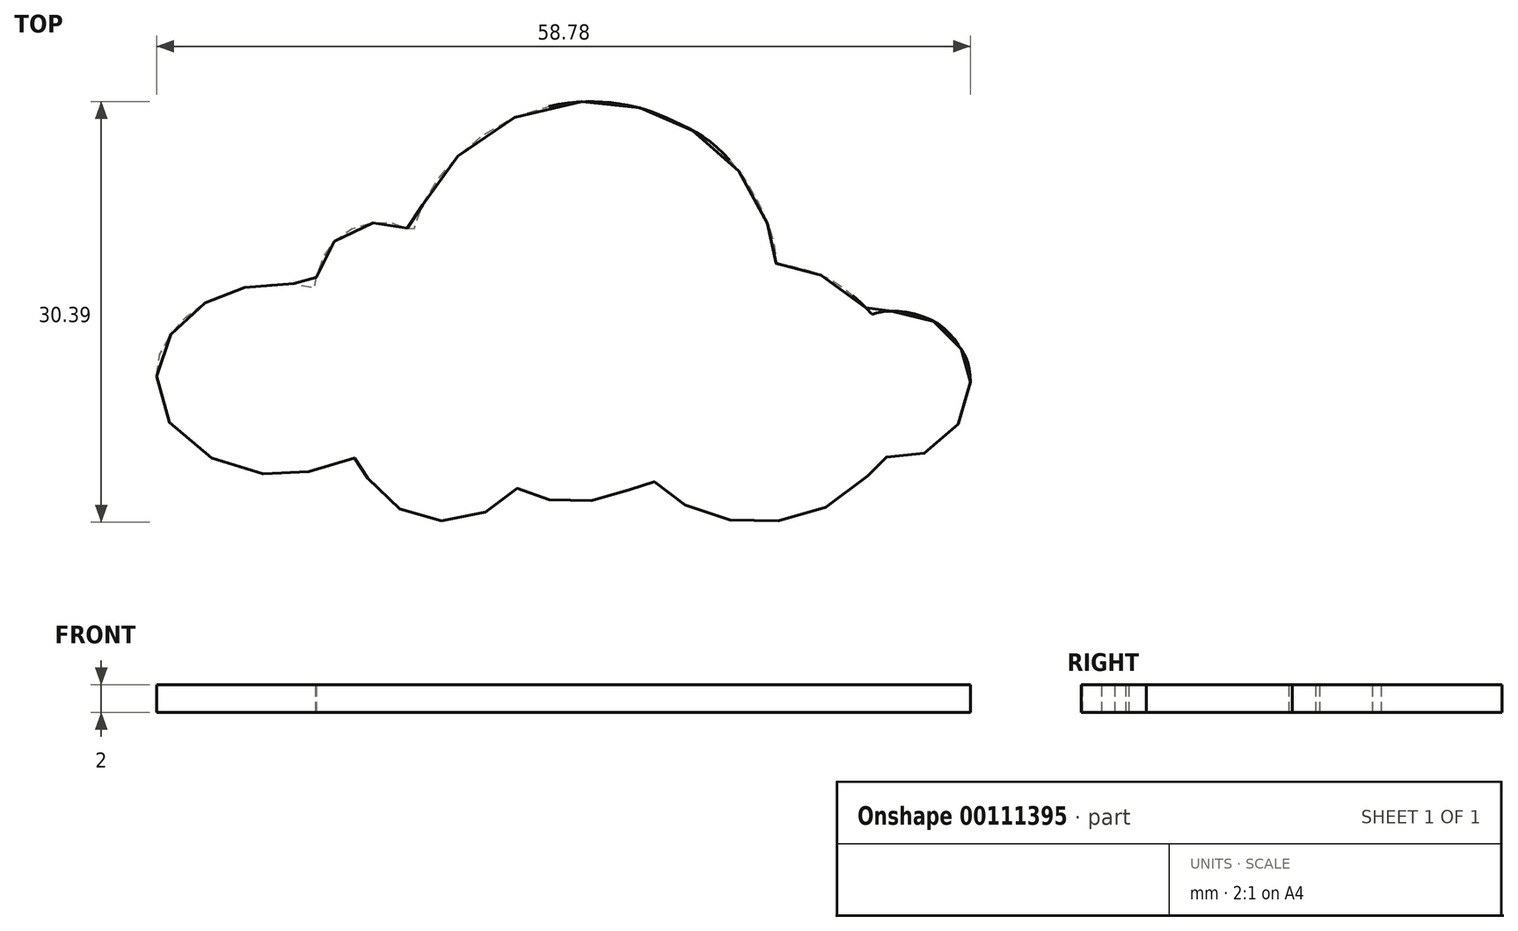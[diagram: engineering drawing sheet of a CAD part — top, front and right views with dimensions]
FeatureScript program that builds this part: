
annotation { "Feature Type Name" : "Feature", "Feature Type Description" : "" }
export const myFeature = defineFeature(function(context is Context, id is Id, definition is map)
    precondition{}
    {
        {
            var Q0;
            Q0=qCreatedBy(makeId("Top.planeOp"),FACE);
            var sketch = newSketch(context, id + "F0", { "sketchPlane" : qUnion([Q0])});
            skFitSpline(sketch, "E0", {"points": [v(-57.84, 21.95) * mm, v(-57.2, 25.65) * mm, v(-55.16, 30.24) * mm, v(-52.61, 33.18) * mm, v(-47.89, 36.11) * mm, v(-43.17, 37) * mm, v(-39.98, 37) * mm, v(-36.4, 35.86) * mm, v(-35, 35.22) * mm, v(-34.5, 34.97) * mm, v(-33.6, 37.77) * mm, v(-29.07, 46.52) * mm, v(-22.76, 53.84) * mm, v(-12.1, 61.38) * mm, v(1.52, 65.61) * mm, v(11.82, 65.98) * mm, v(21.02, 64.32) * mm, v(29.48, 60.83) * mm, v(37.4, 56.23) * mm, v(44.94, 47.95) * mm, v(49.72, 39.49) * mm, v(52.48, 31.58) * mm, v(52.85, 27.9) * mm, v(53.03, 26.98) * mm, v(55.8, 26.61) * mm, v(65.17, 23.67) * mm, v(72.16, 18.7) * mm, v(75.84, 15.02) * mm, v(76.06, 14.83) * mm, v(76.36, 15) * mm, v(79.54, 15.57) * mm, v(84.16, 15.4) * mm, v(89.46, 13.92) * mm, v(93.72, 11.19) * mm, v(96.37, 8.14) * mm, v(98.42, 4.9) * mm, v(99.36, 2.06) * mm, v(99.77, -1.44) * mm, v(98.87, -7.47) * mm, v(95.72, -12.94) * mm, v(91, -17.44) * mm, v(85.84, -19.26) * mm, v(80.69, -19.51) * mm, v(79.03, -19.43) * mm, v(78.44, -19.43) * mm, v(78.2, -19.93) * mm, v(75.29, -23.67) * mm, v(68.72, -29.4) * mm, v(61.66, -32.97) * mm, v(54.36, -34.78) * mm, v(47.09, -35.13) * mm, v(39.82, -34.29) * mm, v(33.17, -32.19) * mm, v(27.72, -28.9) * mm, v(24.23, -26.1) * mm, v(22.97, -24.7) * mm, v(22.4, -24.36) * mm, v(22.06, -24.7) * mm, v(16.41, -27.93) * mm, v(11.93, -29.44) * mm, v(7.48, -30.11) * mm, v(1.73, -30.11) * mm, v(-3.55, -29.4) * mm, v(-8, -27.73) * mm, v(-9.35, -27.05) * mm, v(-9.79, -27.53) * mm, v(-14.1, -31.16) * mm, v(-20.35, -33.88) * mm, v(-26.54, -34.87) * mm, v(-32.64, -34.04) * mm, v(-37.83, -31.82) * mm, v(-43.02, -27.37) * mm, v(-45.99, -23.5) * mm, v(-47.47, -20.03) * mm, v(-47.78, -19.42) * mm, v(-48.17, -19.53) * mm, v(-53.73, -21.68) * mm, v(-60.56, -23.21) * mm, v(-65.36, -23.68) * mm, v(-75.4, -22.76) * mm, v(-82.94, -19.72) * mm, v(-90.86, -13.92) * mm, v(-95.28, -6.56) * mm, v(-96.18, 0) * mm, v(-95.4, 5.26) * mm, v(-92.68, 10.18) * mm, v(-88.5, 14.8) * mm, v(-83.6, 18.09) * mm, v(-78.85, 20.07) * mm, v(-74.24, 21.5) * mm, v(-66.83, 22.21) * mm, v(-61.3, 22.02) * mm, v(-57.73, 21.3) * mm, v(-57.84, 21.95) * mm]});
            skLineSegment(sketch, "E1", {"start": v(-96.18, 0) * mm, "end": v(99.77, -1.44) * mm});
            skSolve(sketch);
        }
        {
            var Q0;
            Q0 = qSketchRegion(id + "F0", true);
            extrude(context, id + "F1", {"entities" : qUnion([Q0]), "depth" : 2 * mm});
        }
        {
            var Q0;
            Q0=makeQuery(id+"F1.opExtrude","SWEPT_BODY",BODY,{"disambiguationData":[OSD([sQuery(id+"F0.wireOp",EDGE,"E0")])]});
            var Q1;
            Q1=qCreatedBy(makeId("Origin.pointOp"),VERTEX);
            transform(context, id + "F2", {"entities" : qUnion([Q0]), "transformType" : TransformType.SCALE_UNIFORMLY, "scale" : 0.3, "scalePoint" : qUnion([Q1]), "makeCopy" : false});
        }
        {
            var Q0;
            Q0=makeQuery(id+"F1.opExtrude","CAP_FACE",FACE,{"disambiguationData":[OSD([sQuery(id+"F0.wireOp",EDGE,"E0")])],"isStart":false});
            extrude(context, id + "F3", {"entities" : qUnion([Q0]), "operationType" : NewBodyOperationType.ADD, "depth" : 1.4 * mm});
        }
    });
